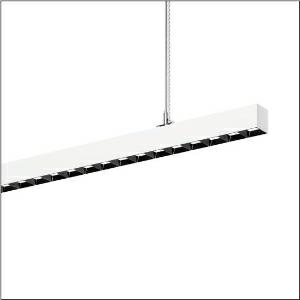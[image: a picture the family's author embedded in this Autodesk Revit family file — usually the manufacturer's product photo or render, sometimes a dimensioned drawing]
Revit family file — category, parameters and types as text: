
# Revit family: silica_r__21_51mx32tctdw_3fbf
name_source: partatom
category: Lighting Fixtures
units: mm (PartAtom-declared; Revit-internal decimal feet)

## family parameters
Cut with Voids When Loaded = No
Host = Face
Light Source = No
Part Type = Normal
Room Calculation Point = No
Round Connector Dimension = Use Diameter
Shared = No

## types (1)
- --- (1 x LED, 15540 lm, 133.6 W, 6500K)
    Apparent Load = 134 VA
    CIE Flux Codes = 84 99 100 60 100
    Color Rendering = 80
    Color Temperature = 6500K
    Default Elevation = 1800 mm
    Description = Silica® 21, office luminaire, primary light control with darklight reflector, of PMMA, black, CAT 2 (L<= 3000cd/m²), light emission: direct/indirect distribution, primary light characteristic: symmetric, installation type: suspended mounting, LED, rated luminous flux: 15.540lm, luminous efficacy: 111lm/W, light colour: 8tw, colour temperature: 2700..6500K, control gear: ECG DALI, with terminal, 3+2-pole, max. 2.5mm², mains connection: 220..240V, AC, 50/60Hz, rated input power: 140.3W, luminaire housing, of aluminium, traffic white (RAL 9016), length: 3.004mm, width: 53mm, height: 53mm, protection rating (complete): IP20, insulation class (complete): insulation class I (protective earthing), certification: CE, permissible operating ambient temperature: 0..+35°C, standard: EN 50419, packaging unit: 1 piece
    Height = 53 mm
    Lamp = 1 x LED
    Lamp Light Flux = 15540 lm
    Lamp Power = 133.6 W
    Lamp count = 1
    Length = 3004 mm
    Luminous efficacy = 116 lm/W
    Manufacturer = Siteco
    ModVariant = No
    Model = 51MX32TCTDW
    Mounting Place = Ceiling
    Mounting Type = Pendant
    Number of Poles = 1
    OnlyDefault = Yes
    Power Factor = 1
    Product Name = Silica® 21
    Product group = office luminaire | ceiling pendant
    ProductGroupID = 905
    Protection Class = Protection class I
    Protection Degree = IP 20
    RLX_Detail_Level = 1
    RlxData = <blob elided: 61605 chars, md5=ad3530f1>
    Socket = socket
    Standby Power = 0 W
    System Light Flux = 15540 lm
    System Power = 134 W
    Type Comments = individual setting
    Type Image = l_1251637.jpg
    URL = http://relux.com
    VarID = @adj_046041
    Voltage = 0 V
    Weight = 0.00 kg
    Width = 53 mm

## geometry (parser evidence)
native form markers: Blend x4, Sweep x14
no freeform markers — native parametric forms only
